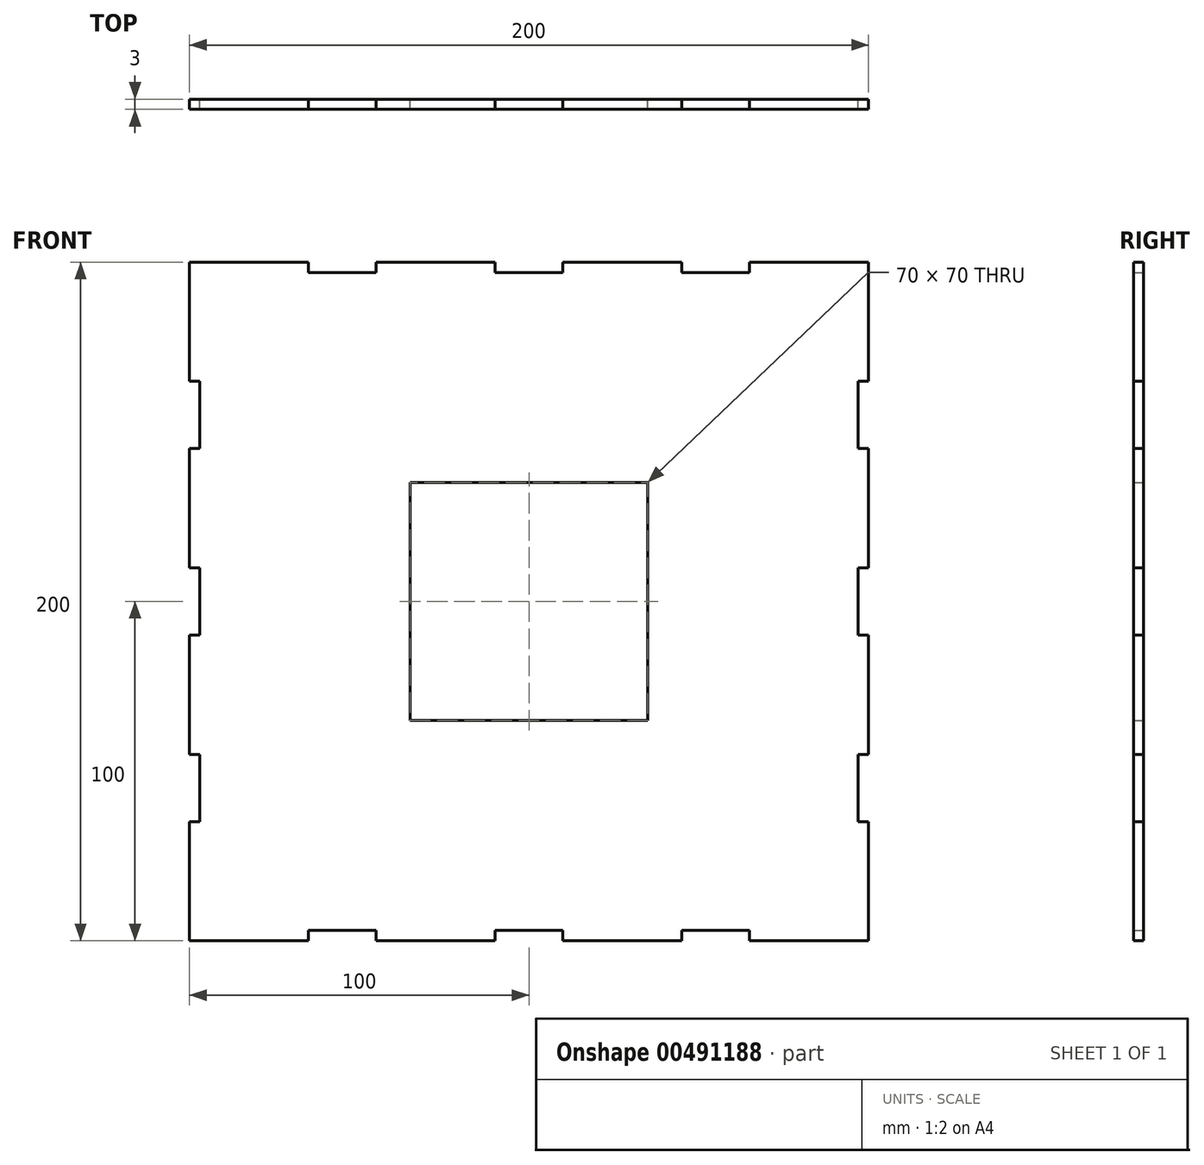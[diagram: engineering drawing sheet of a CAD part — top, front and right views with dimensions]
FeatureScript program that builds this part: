
annotation { "Feature Type Name" : "Feature", "Feature Type Description" : "" }
export const myFeature = defineFeature(function(context is Context, id is Id, definition is map)
    precondition{}
    {
        {
            var Q0;
            Q0=qCreatedBy(makeId("Front.planeOp"),FACE);
            var sketch = newSketch(context, id + "F0", { "sketchPlane" : qUnion([Q0])});
            skLineSegment(sketch, "E0.bottom", {"start": v(100, -100) * mm, "end": v(-100, -100) * mm});
            skLineSegment(sketch, "E0.top", {"start": v(100, 100) * mm, "end": v(-100, 100) * mm});
            skLineSegment(sketch, "E0.left", {"start": v(100, -100) * mm, "end": v(100, 100) * mm});
            skLineSegment(sketch, "E0.right", {"start": v(-100, -100) * mm, "end": v(-100, 100) * mm});
            skPoint(sketch, "E0.middle", {"position": v(0, 0) * mm});
            skLineSegment(sketch, "E1.bottom", {"start": v(-45.03, -100) * mm, "end": v(-64.93, -100) * mm});
            skLineSegment(sketch, "E1.top", {"start": v(-45.03, -96.95) * mm, "end": v(-64.93, -96.95) * mm});
            skLineSegment(sketch, "E1.left", {"start": v(-45.03, -100) * mm, "end": v(-45.03, -96.95) * mm});
            skLineSegment(sketch, "E1.right", {"start": v(-64.93, -100) * mm, "end": v(-64.93, -96.95) * mm});
            skPoint(sketch, "E1.middle", {"position": v(-54.98, -98.47) * mm});
            skLineSegment(sketch, "E2.bottom", {"start": v(45.02, -100) * mm, "end": v(64.92, -100) * mm});
            skLineSegment(sketch, "E2.top", {"start": v(45.02, -96.95) * mm, "end": v(64.92, -96.95) * mm});
            skLineSegment(sketch, "E2.left", {"start": v(45.02, -100) * mm, "end": v(45.02, -96.95) * mm});
            skLineSegment(sketch, "E2.right", {"start": v(64.92, -100) * mm, "end": v(64.92, -96.95) * mm});
            skPoint(sketch, "E2.middle", {"position": v(54.97, -98.48) * mm});
            skLineSegment(sketch, "E3.bottom", {"start": v(9.95, -100) * mm, "end": v(-9.95, -100) * mm});
            skLineSegment(sketch, "E3.top", {"start": v(9.95, -96.95) * mm, "end": v(-9.95, -96.95) * mm});
            skLineSegment(sketch, "E3.left", {"start": v(9.95, -100) * mm, "end": v(9.95, -96.95) * mm});
            skLineSegment(sketch, "E3.right", {"start": v(-9.95, -100) * mm, "end": v(-9.95, -96.95) * mm});
            skPoint(sketch, "E3.middle", {"position": v(0, -98.47) * mm});
            skLineSegment(sketch, "E4.bottom", {"start": v(-100, -45.03) * mm, "end": v(-96.95, -45.03) * mm});
            skLineSegment(sketch, "E4.top", {"start": v(-100, -64.93) * mm, "end": v(-96.95, -64.93) * mm});
            skLineSegment(sketch, "E4.left", {"start": v(-100, -45.03) * mm, "end": v(-100, -64.93) * mm});
            skLineSegment(sketch, "E4.right", {"start": v(-96.95, -45.03) * mm, "end": v(-96.95, -64.93) * mm});
            skPoint(sketch, "E4.middle", {"position": v(-98.48, -54.98) * mm});
            skLineSegment(sketch, "E5.bottom", {"start": v(-96.95, -9.95) * mm, "end": v(-100, -9.95) * mm});
            skLineSegment(sketch, "E5.top", {"start": v(-96.95, 9.95) * mm, "end": v(-100, 9.95) * mm});
            skLineSegment(sketch, "E5.left", {"start": v(-96.95, -9.95) * mm, "end": v(-96.95, 9.95) * mm});
            skLineSegment(sketch, "E5.right", {"start": v(-100, -9.95) * mm, "end": v(-100, 9.95) * mm});
            skPoint(sketch, "E5.middle", {"position": v(-98.48, 0) * mm});
            skLineSegment(sketch, "E6.bottom", {"start": v(-96.95, 45.02) * mm, "end": v(-100, 45.02) * mm});
            skLineSegment(sketch, "E6.top", {"start": v(-96.95, 64.92) * mm, "end": v(-100, 64.92) * mm});
            skLineSegment(sketch, "E6.left", {"start": v(-96.95, 45.02) * mm, "end": v(-96.95, 64.92) * mm});
            skLineSegment(sketch, "E6.right", {"start": v(-100, 45.02) * mm, "end": v(-100, 64.92) * mm});
            skPoint(sketch, "E6.middle", {"position": v(-98.48, 54.97) * mm});
            skLineSegment(sketch, "E7.bottom", {"start": v(100, 45.03) * mm, "end": v(96.95, 45.03) * mm});
            skLineSegment(sketch, "E7.top", {"start": v(100, 64.93) * mm, "end": v(96.95, 64.93) * mm});
            skLineSegment(sketch, "E7.left", {"start": v(100, 45.03) * mm, "end": v(100, 64.93) * mm});
            skLineSegment(sketch, "E7.right", {"start": v(96.95, 45.03) * mm, "end": v(96.95, 64.93) * mm});
            skPoint(sketch, "E7.middle", {"position": v(98.48, 54.98) * mm});
            skLineSegment(sketch, "E8.bottom", {"start": v(100, -9.95) * mm, "end": v(96.95, -9.95) * mm});
            skLineSegment(sketch, "E8.top", {"start": v(100, 9.95) * mm, "end": v(96.95, 9.95) * mm});
            skLineSegment(sketch, "E8.left", {"start": v(100, -9.95) * mm, "end": v(100, 9.95) * mm});
            skLineSegment(sketch, "E8.right", {"start": v(96.95, -9.95) * mm, "end": v(96.95, 9.95) * mm});
            skPoint(sketch, "E8.middle", {"position": v(98.47, 0) * mm});
            skLineSegment(sketch, "E9.bottom", {"start": v(100, -64.92) * mm, "end": v(96.95, -64.92) * mm});
            skLineSegment(sketch, "E9.top", {"start": v(100, -45.02) * mm, "end": v(96.95, -45.02) * mm});
            skLineSegment(sketch, "E9.left", {"start": v(100, -64.92) * mm, "end": v(100, -45.02) * mm});
            skLineSegment(sketch, "E9.right", {"start": v(96.95, -64.92) * mm, "end": v(96.95, -45.02) * mm});
            skPoint(sketch, "E9.middle", {"position": v(98.47, -54.97) * mm});
            skLineSegment(sketch, "E10.bottom", {"start": v(-45.03, 100) * mm, "end": v(-64.93, 100) * mm});
            skLineSegment(sketch, "E10.top", {"start": v(-45.03, 96.95) * mm, "end": v(-64.93, 96.95) * mm});
            skLineSegment(sketch, "E10.left", {"start": v(-45.03, 100) * mm, "end": v(-45.03, 96.95) * mm});
            skLineSegment(sketch, "E10.right", {"start": v(-64.93, 100) * mm, "end": v(-64.93, 96.95) * mm});
            skPoint(sketch, "E10.middle", {"position": v(-54.98, 98.47) * mm});
            skLineSegment(sketch, "E11.bottom", {"start": v(9.95, 96.95) * mm, "end": v(-9.95, 96.95) * mm});
            skLineSegment(sketch, "E11.top", {"start": v(9.95, 100) * mm, "end": v(-9.95, 100) * mm});
            skLineSegment(sketch, "E11.left", {"start": v(9.95, 96.95) * mm, "end": v(9.95, 100) * mm});
            skLineSegment(sketch, "E11.right", {"start": v(-9.95, 96.95) * mm, "end": v(-9.95, 100) * mm});
            skPoint(sketch, "E11.middle", {"position": v(0, 98.48) * mm});
            skLineSegment(sketch, "E12.bottom", {"start": v(64.93, 96.95) * mm, "end": v(45.03, 96.95) * mm});
            skLineSegment(sketch, "E12.top", {"start": v(64.93, 100) * mm, "end": v(45.03, 100) * mm});
            skLineSegment(sketch, "E12.left", {"start": v(64.93, 96.95) * mm, "end": v(64.93, 100) * mm});
            skLineSegment(sketch, "E12.right", {"start": v(45.03, 96.95) * mm, "end": v(45.03, 100) * mm});
            skPoint(sketch, "E12.middle", {"position": v(54.98, 98.48) * mm});
            skLineSegment(sketch, "E13.bottom", {"start": v(35, -35) * mm, "end": v(-35, -35) * mm});
            skLineSegment(sketch, "E13.top", {"start": v(35, 35) * mm, "end": v(-35, 35) * mm});
            skLineSegment(sketch, "E13.left", {"start": v(35, -35) * mm, "end": v(35, 35) * mm});
            skLineSegment(sketch, "E13.right", {"start": v(-35, -35) * mm, "end": v(-35, 35) * mm});
            skSolve(sketch);
        }
        {
            var Q0;
            Q0=makeQuery(id+"F0.imprint","IMPRINT",FACE,{"disambiguationData":[TD([[makeQuery(id+"F0.imprint","IMPRINT",EDGE,{"derivedFrom":sQuery(id+"F0.wireOp",EDGE,"E0.top")}),1.0]])]});
            extrude(context, id + "F1", {"entities" : qUnion([Q0]), "depth" : 3 * mm});
        }
    });
